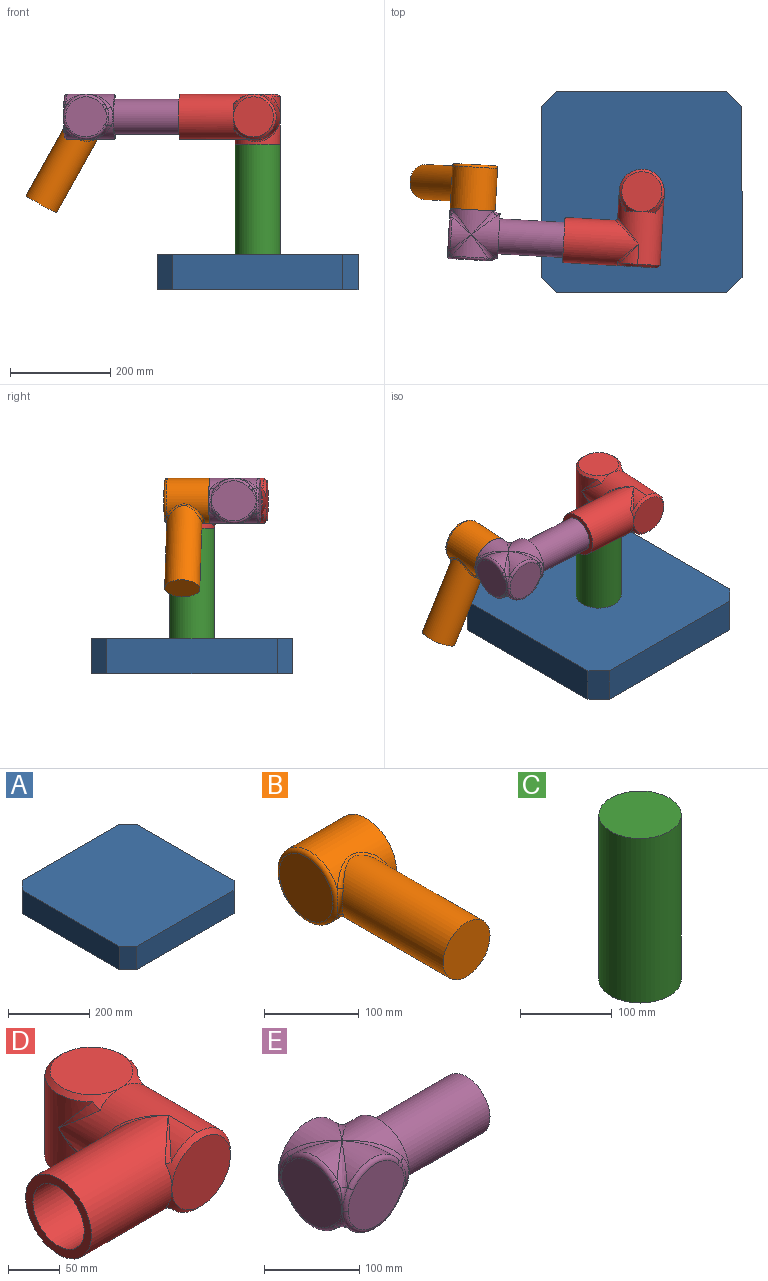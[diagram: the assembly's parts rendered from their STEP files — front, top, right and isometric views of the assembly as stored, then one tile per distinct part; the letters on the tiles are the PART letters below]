
ASSEMBLY  parts=5 mates=9
PART A: 10 faces, bbox 400x400x70 mm
  f0: plane 340x70mm, normal (1,0,0), area 23800mm2, adj f4,f5,f8,f9
  f1: plane 340x70mm, normal (0,1,0), area 23800mm2, adj f4,f5,f6,f8
  f2: plane 340x70mm, normal (-1,0,0), area 23800mm2, adj f4,f5,f6,f7
  f3: plane 340x70mm, normal (0,-1,0), area 23800mm2, adj f4,f5,f7,f9
  f4: plane 400x400mm, normal (0,0,1), area 158200mm2, adj f0,f1,f2,f3,f6,f7,f8,f9
  f5: plane 400x400mm, normal (0,0,-1), area 158200mm2, adj f0,f1,f2,f3,f6,f7,f8,f9
  f6: plane 70x30mm, normal (-0.71,0.71,0), area 2969.8mm2, adj f1,f2,f4,f5
  f7: plane 70x30mm, normal (-0.71,-0.71,0), area 2969.8mm2, adj f2,f3,f4,f5
  f8: plane 70x30mm, normal (0.71,0.71,0), area 2969.8mm2, adj f0,f1,f4,f5
  f9: plane 70x30mm, normal (0.71,-0.71,0), area 2969.8mm2, adj f0,f3,f4,f5
PART B: 8 faces, bbox 90x248.7x97.4 mm
  f0: cylinder r=45mm len=90mm, axis (1,0,0), area 19134.3mm2, adj f2,f5,f7
  f1: plane 80x80mm, normal (-1,0,0), area 5026.5mm2, adj f5
  f2: plane 90x90mm, normal (1,0,0), area 6361.7mm2, adj f0
  f3: cylinder r=35mm len=170.01mm, axis (0,1,0), area 35073mm2, adj f4,f6,f7
  f4: plane 70x70mm, normal (0,-1,0), area 3848.5mm2, adj f3
  f5: torus R=40mm, axis (1,0,0), area 2069.1mm2, adj f0,f1,f6
  f6: bspline ~38.74x8.08mm, area 205.8mm2, adj f3,f5,f7
  f7: bspline ~74.94x72mm, area 1080.9mm2, adj f0,f3,f6
PART C: 3 faces, bbox 90x90x220 mm
  f0: cylinder r=45mm len=220mm, axis (0,0,-1), area 62203.5mm2, adj f1,f2
  f1: plane 90x90mm, normal (0,0,1), area 6361.7mm2, adj f0
  f2: plane 90x90mm, normal (0,0,-1), area 6361.7mm2, adj f0
PART D: 20 faces, bbox 201x201x103.7 mm
  f0: cylinder r=45mm len=95mm, axis (0,0,-1), area 17438.7mm2, adj f1,f15,f17,f18,f19
  f1: cylinder r=45mm len=40mm, axis (0,0,-1), area 732.9mm2, adj f0,f2,f15
  f2: bspline ~48.66x48.66mm, area 192.8mm2, adj f1,f3,f15
  f3: cylinder r=45mm len=145mm, axis (0,1,0), area 22953.4mm2, adj f2,f4,f11,f12,f13,f15,f17,f18
  f4: cylinder r=45mm len=40mm, axis (0,1,0), area 834.6mm2, adj f3,f5,f10,f13
  f5: bspline ~30.38x30.38mm, area 20.4mm2, adj f4,f6
  f6: cylinder r=45mm len=150mm, axis (1,0,0), area 33919mm2, adj f5,f7,f10,f11,f12,f13
  f7: plane 90x90mm, normal (-1,0,0), area 2513.3mm2, adj f6,f8
  f8: cylinder r=35mm len=130mm, axis (-1,0,0), area 28588.5mm2, adj f7,f9
  f9: plane 70x70mm, normal (-1,0,0), area 3848.5mm2, adj f8
  f10: bspline ~36.53x36.53mm, area 63.4mm2, adj f4,f6,f13
  f11: bspline ~90x50mm, area 606.6mm2, adj f3,f6
  f12: bspline ~44.88x44.88mm, area 113.3mm2, adj f3,f6,f13
  f13: cone r=40mm half-angle=45deg, axis (0,1,0), area 1721.5mm2, adj f3,f4,f6,f10,f12,f14
  f14: plane 80x80mm, normal (0,-1,0), area 5026.5mm2, adj f13
  f15: cone r=40mm half-angle=45deg, axis (0,0,-1), area 1788.9mm2, adj f0,f1,f2,f3,f16,f17
  f16: plane 80x80mm, normal (0,0,1), area 5026.5mm2, adj f15
  f17: bspline ~48.66x48.66mm, area 195.6mm2, adj f0,f3,f15
  f18: bspline ~90x50mm, area 786.3mm2, adj f0,f3
  f19: plane 90x90mm, normal (0,0,-1), area 6361.7mm2, adj f0
PART E: 44 faces, bbox 232.9x104.1x98.5 mm
  f0: cylinder r=45mm len=73.64mm, axis (0,1,0), area 1940.4mm2, adj f1,f41,f42,f43
  f1: bspline ~46.73x46.73mm, area 368.3mm2, adj f0,f2,f39,f40
  f2: bspline ~27.69x13.49mm, area 74.2mm2, adj f1,f3,f38
  f3: bspline ~28.09x13.7mm, area 185.3mm2, adj f2,f4,f37,f41
  f4: plane 82.49x80mm, normal (0,-1,0), area 5110.1mm2, adj f3,f5,f34,f35,f36,f37,f41
  f5: torus R=40mm, axis (0,-1,0), area 650mm2, adj f4,f6,f34,f37
  f6: cylinder r=45mm len=73.64mm, axis (0,1,0), area 1940.4mm2, adj f5,f7,f33
  f7: bspline ~51.5x51.5mm, area 303.7mm2, adj f6,f8,f9,f34
  f8: bspline ~40.18x13.53mm, area 322mm2, adj f7,f9,f35,f42
  f9: cylinder r=45mm len=90mm, axis (1,0,0), area 6548.7mm2, adj f7,f8,f10,f28,f29,f30,f42,f43
  f10: bspline ~51.5x51.5mm, area 134.3mm2, adj f9,f11,f28
  f11: cylinder r=45mm len=90mm, axis (0,-1,0), area 5214.8mm2, adj f10,f12,f24,f25,f26,f27,f29
  f12: bspline ~46.73x46.73mm, area 231.4mm2, adj f11,f13,f23,f24
  f13: bspline ~19.73x18.67mm, area 60mm2, adj f12,f14,f21,f22
  f14: plane 91.13x81.13mm, normal (-1,0,0), area 5353.4mm2, adj f13,f15,f16,f17,f18,f19,f21,f22
  f15: torus R=40mm, axis (1,0,0), area 552.4mm2, adj f14,f16,f39,f40
  f16: bspline ~17.82x17.17mm, area 60mm2, adj f14,f15,f17,f26
  f17: bspline ~26.85x11.76mm, area 69.8mm2, adj f14,f16,f25
  f18: bspline ~17.82x17.17mm, area 60mm2, adj f14,f19,f22,f33
  f19: bspline ~26.85x11.76mm, area 69.8mm2, adj f14,f18,f20
  f20: bspline ~25.87x10.42mm, area 78mm2, adj f19,f33,f37
  f21: bspline ~26.85x11.76mm, area 48mm2, adj f13,f14,f24
  f22: torus R=40mm, axis (1,0,0), area 552.4mm2, adj f13,f14,f18,f23
  f23: cylinder r=45mm len=65.45mm, axis (1,0,0), area 1465.8mm2, adj f12,f22,f33
  f24: bspline ~27.69x13.49mm, area -31.9mm2, adj f11,f12,f21
  f25: bspline ~27.69x13.49mm, area -31.9mm2, adj f11,f17,f26
  f26: bspline ~46.73x46.73mm, area 129.6mm2, adj f11,f16,f25,f40
  f27: plane 90.57x90.57mm, normal (0,1,0), area 6361.7mm2, adj f11,f28
  f28: bspline ~39.65x13.53mm, area 437.2mm2, adj f9,f10,f27,f29
  f29: bspline ~51.5x51.5mm, area 320.1mm2, adj f9,f11,f28
  f30: plane 90x90mm, normal (1,0,0), area 2513.3mm2, adj f9,f31
  f31: cylinder r=35mm len=130mm, axis (1,0,0), area 28588.5mm2, adj f30,f32
  f32: plane 70x70mm, normal (1,0,0), area 3848.5mm2, adj f31
  f33: bspline ~46.73x46.73mm, area 266.4mm2, adj f6,f18,f20,f23
  f34: bspline ~17.71x13.7mm, area 67.2mm2, adj f4,f5,f7,f35
  f35: bspline ~40.34x9.54mm, area 168.5mm2, adj f4,f8,f34,f36
  f36: bspline ~17.71x13.7mm, area 67.2mm2, adj f4,f35,f41,f42
  f37: bspline ~26.43x12.63mm, area 185.3mm2, adj f3,f4,f5,f20
  f38: bspline ~26.85x11.75mm, area 48.6mm2, adj f2,f14,f39
  f39: bspline ~19.73x18.67mm, area 60mm2, adj f1,f14,f15,f38
  f40: cylinder r=45mm len=65.45mm, axis (1,0,0), area 1465.8mm2, adj f1,f15,f26
  f41: torus R=40mm, axis (0,-1,0), area 650mm2, adj f0,f3,f4,f36
  f42: bspline ~48.56x48.56mm, area 327.4mm2, adj f0,f8,f9,f36
  f43: bspline ~12.5x12.5mm, area 0.3mm2, adj f0,f9
PLACE A rot(axis=(0,0,-1),90deg) t=(0,200,-35)mm
PLACE B rot(axis=(0.43,-0.46,-0.78),107.4deg) t=(-337.58,164.09,310)mm
PLACE C t=(0,200,35)mm
PLACE D rot(axis=(0,0,-1),3.3deg) t=(0,200,255)mm
PLACE E rot(axis=(0,0,-1),3.3deg) t=(-155.71,103.68,310)mm
MATE planar C.f0 <-> D.f0  axis (0,0,1) through (0,200,255)mm
MATE cylindrical D.f0 <-> C.f0  axis (0,0,-1) through (0,200,255)mm
MATE parallel E.f31 <-> D.f6  axis (1,-0.06,0) through (-155.71,103.68,310)mm
MATE cylindrical E.f31 <-> D.f6  axis (1,-0.06,0) through (-155.71,103.68,310)mm
MATE parallel E.f0 <-> D.f3  axis (-0.06,-1,0) through (-343.25,64.25,310)mm
MATE planar A.f4 <-> C.f0  axis (0,0,1) through (0,200,35)mm
MATE cylindrical B.f0 <-> E.f0  axis (-0.06,-1,0) through (-337.58,164.09,310)mm
MATE cylindrical C.f0 <-> A.f4  axis (0,0,-1) through (0,200,35)mm
MATE planar E.f0 <-> B.f0  axis (0.06,1,0) through (-337.58,164.09,310)mm
